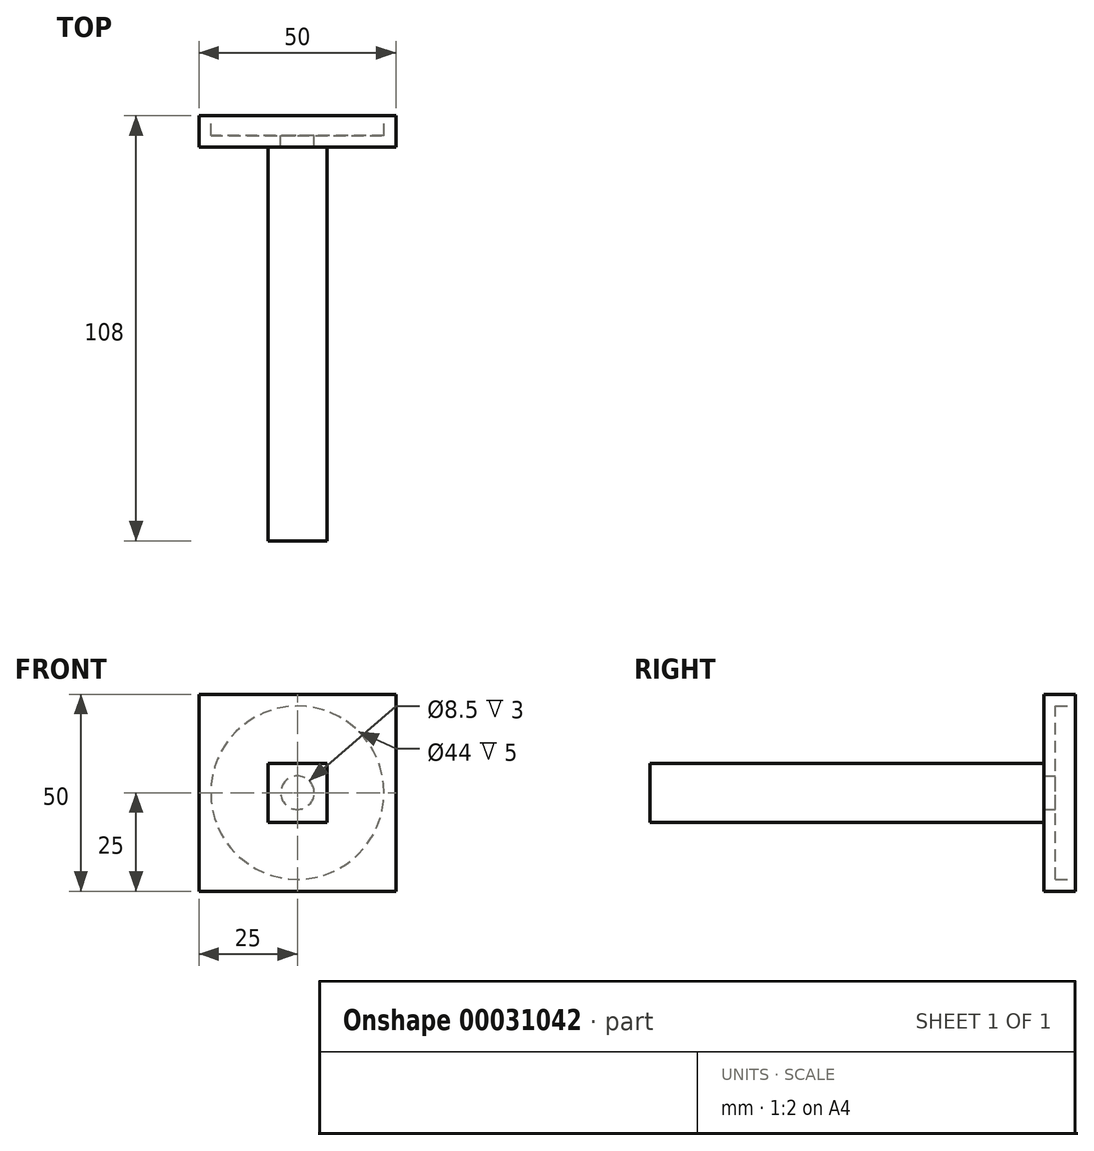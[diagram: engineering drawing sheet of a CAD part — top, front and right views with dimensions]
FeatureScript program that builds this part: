
annotation { "Feature Type Name" : "Feature", "Feature Type Description" : "" }
export const myFeature = defineFeature(function(context is Context, id is Id, definition is map)
    precondition{}
    {
        {
            var Q0;
            Q0=qCreatedBy(makeId("Front.planeOp"),FACE);
            var sketch = newSketch(context, id + "F0", { "sketchPlane" : qUnion([Q0])});
            skLineSegment(sketch, "E0.rect.bottom", {"start": v(25, -25) * mm, "end": v(-25, -25) * mm});
            skLineSegment(sketch, "E0.rect.top", {"start": v(25, 25) * mm, "end": v(-25, 25) * mm});
            skLineSegment(sketch, "E0.rect.left", {"start": v(25, -25) * mm, "end": v(25, 25) * mm});
            skLineSegment(sketch, "E0.rect.right", {"start": v(-25, -25) * mm, "end": v(-25, 25) * mm});
            skPoint(sketch, "E0.rect.middle", {"position": v(0, 0) * mm});
            skCircle(sketch, "E1", {"center": v(0, 0) * mm, "radius": 4.25 * mm});
            skSolve(sketch);
        }
        {
            var Q0;
            Q0 = qSketchRegion(id + "F0", true);
            extrude(context, id + "F1", {"entities" : qUnion([Q0]), "depth" : 8 * mm});
        }
        {
            var Q0;
            Q0=qCreatedBy(makeId("Front.planeOp"),FACE);
            var sketch = newSketch(context, id + "F2", { "sketchPlane" : qUnion([Q0])});
            skCircle(sketch, "E2", {"center": v(0, 0) * mm, "radius": 22 * mm});
            skSolve(sketch);
        }
        {
            var Q0;
            Q0 = qSketchRegion(id + "F2", true);
            extrude(context, id + "F3", {"entities" : qUnion([Q0]), "operationType" : NewBodyOperationType.REMOVE, "depth" : 5 * mm});
        }
        {
            var Q0;
            Q0=makeQuery(id+"F1.opExtrude","CAP_FACE",FACE,{"disambiguationData":[OSD([sQuery(id+"F0.wireOp",EDGE,"E0.rect.bottom"),sQuery(id+"F0.wireOp",EDGE,"E0.rect.top"),sQuery(id+"F0.wireOp",EDGE,"E0.rect.left"),sQuery(id+"F0.wireOp",EDGE,"E0.rect.right"),sQuery(id+"F0.wireOp",EDGE,"E1")])],"isStart":false});
            var sketch = newSketch(context, id + "F4", { "sketchPlane" : qUnion([Q0])});
            skLineSegment(sketch, "E3.rect.bottom", {"start": v(7.5, -7.5) * mm, "end": v(-7.5, -7.5) * mm});
            skLineSegment(sketch, "E3.rect.top", {"start": v(7.5, 7.5) * mm, "end": v(-7.5, 7.5) * mm});
            skLineSegment(sketch, "E3.rect.left", {"start": v(7.5, -7.5) * mm, "end": v(7.5, 7.5) * mm});
            skLineSegment(sketch, "E3.rect.right", {"start": v(-7.5, -7.5) * mm, "end": v(-7.5, 7.5) * mm});
            skPoint(sketch, "E3.rect.middle", {"position": v(0, 0) * mm});
            skSolve(sketch);
        }
        {
            var Q0;
            Q0 = qSketchRegion(id + "F4", true);
            extrude(context, id + "F5", {"entities" : qUnion([Q0]), "operationType" : NewBodyOperationType.ADD, "depth" : 100 * mm});
        }
    });
